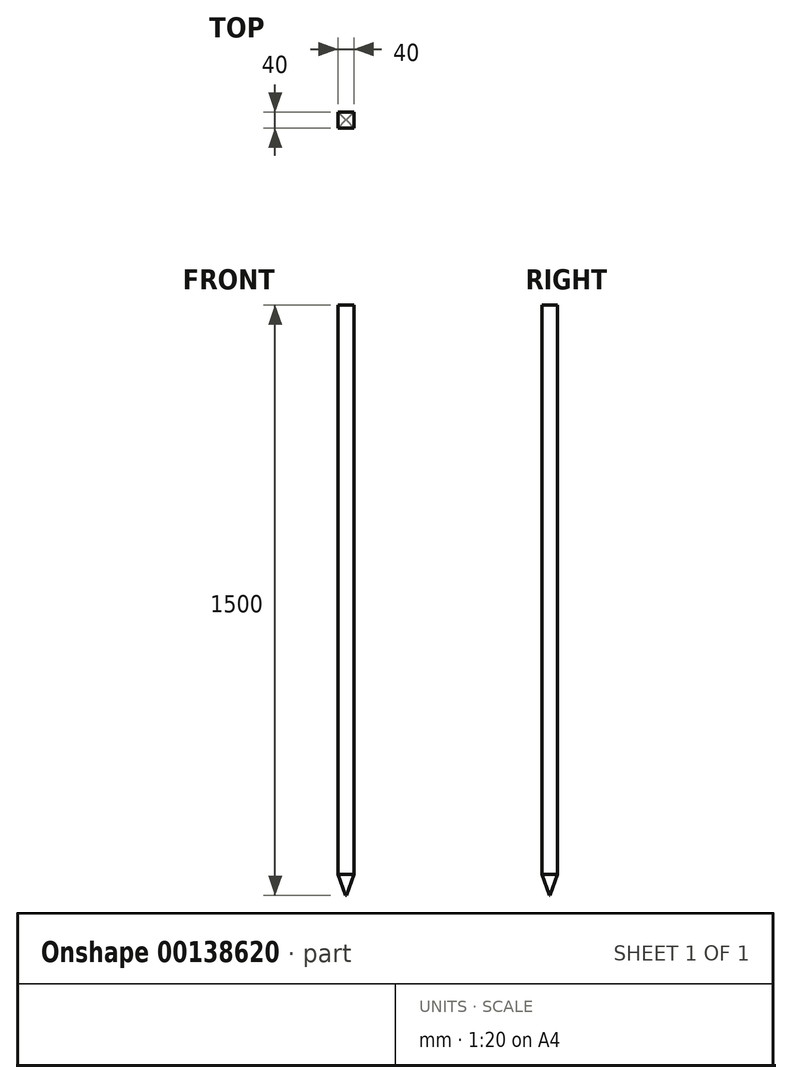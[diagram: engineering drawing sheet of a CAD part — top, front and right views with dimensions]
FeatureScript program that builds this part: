
annotation { "Feature Type Name" : "Feature", "Feature Type Description" : "" }
export const myFeature = defineFeature(function(context is Context, id is Id, definition is map)
    precondition{}
    {
        {
            var Q0;
            Q0=qCreatedBy(makeId("Top.planeOp"),FACE);
            var sketch = newSketch(context, id + "F0", { "sketchPlane" : qUnion([Q0])});
            skLineSegment(sketch, "E0.bottom", {"start": v(20, 20) * mm, "end": v(-20, 20) * mm});
            skLineSegment(sketch, "E0.top", {"start": v(20, -20) * mm, "end": v(-20, -20) * mm});
            skLineSegment(sketch, "E0.left", {"start": v(20, 20) * mm, "end": v(20, -20) * mm});
            skLineSegment(sketch, "E0.right", {"start": v(-20, 20) * mm, "end": v(-20, -20) * mm});
            skPoint(sketch, "E0.middle", {"position": v(0, 0) * mm});
            skSolve(sketch);
        }
        {
            var Q0;
            Q0 = qSketchRegion(id + "F0", true);
            extrude(context, id + "F1", {"entities" : qUnion([Q0]), "oppositeDirection" : true, "depth" : 1500 * mm});
        }
        {
            var Q0;
            Q0=makeQuery(id+"F1.opExtrude","CAP_EDGE",EDGE,{"disambiguationData":[OSD([sQuery(id+"F0.wireOp",EDGE,"E0.top")])],"isStart":false});
            var Q1;
            Q1=makeQuery(id+"F1.opExtrude","CAP_EDGE",EDGE,{"disambiguationData":[OSD([sQuery(id+"F0.wireOp",EDGE,"E0.left")])],"isStart":false});
            var Q2;
            Q2=makeQuery(id+"F1.opExtrude","CAP_EDGE",EDGE,{"disambiguationData":[OSD([sQuery(id+"F0.wireOp",EDGE,"E0.bottom")])],"isStart":false});
            var Q3;
            Q3=makeQuery(id+"F1.opExtrude","CAP_EDGE",EDGE,{"disambiguationData":[OSD([sQuery(id+"F0.wireOp",EDGE,"E0.right")])],"isStart":false});
            chamfer(context, id + "F2", {"entities" : qUnion([Q0, Q1, Q2, Q3]), "chamferType" : ChamferType.OFFSET_ANGLE, "width" : 53 * mm, "oppositeDirection" : true, "angle" : 20 * degree, "tangentPropagation" : true});
        }
    });
